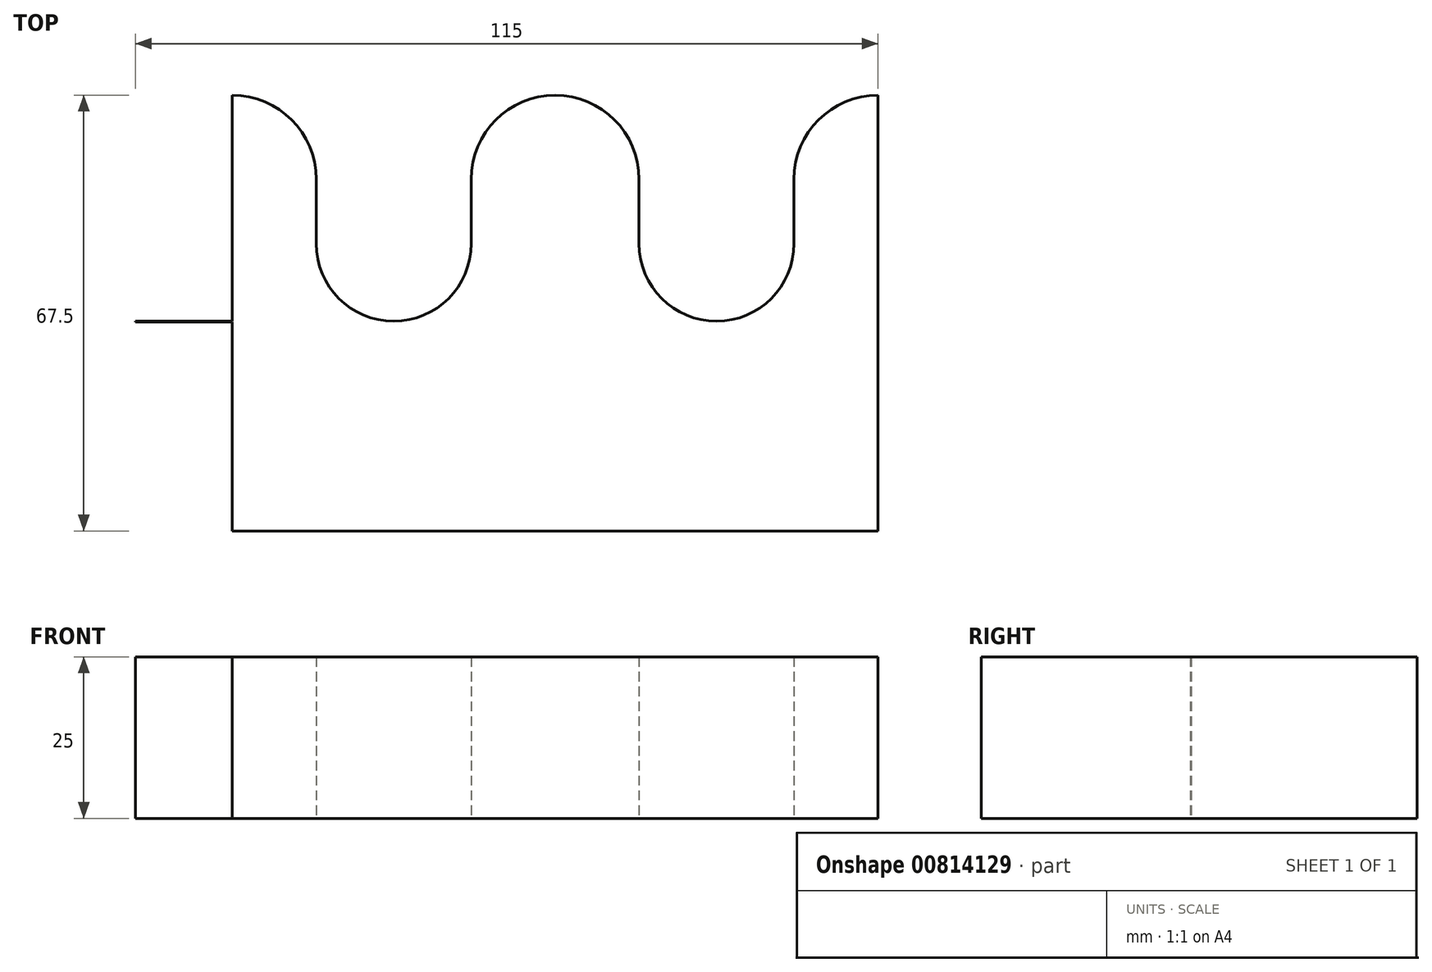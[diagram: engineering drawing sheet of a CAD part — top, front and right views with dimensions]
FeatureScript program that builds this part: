
annotation { "Feature Type Name" : "Feature", "Feature Type Description" : "" }
export const myFeature = defineFeature(function(context is Context, id is Id, definition is map)
    precondition{}
    {
        {
            var Q0;
            Q0=qCreatedBy(makeId("Top.planeOp"),FACE);
            var sketch = newSketch(context, id + "F0", { "sketchPlane" : qUnion([Q0])});
            skLineSegment(sketch, "E0", {"start": v(0, 0) * mm, "end": v(0, -67.5) * mm});
            skLineSegment(sketch, "E1", {"start": v(0, -67.5) * mm, "end": v(100, -67.5) * mm});
            skLineSegment(sketch, "E2", {"start": v(100, -67.5) * mm, "end": v(100, 0) * mm});
            skArc(sketch, "E3", {"start": v(0, 0) * mm, "mid": v(9.2, -3.8) * mm, "end": v(13, -13) * mm});
            skLineSegment(sketch, "E4", {"start": v(13, -13) * mm, "end": v(13, -23) * mm});
            skArc(sketch, "E5", {"start": v(13, -23) * mm, "mid": v(25, -35) * mm, "end": v(37, -23) * mm});
            skLineSegment(sketch, "E6", {"start": v(37, -23) * mm, "end": v(37, -13) * mm});
            skArc(sketch, "E7", {"start": v(63, -13) * mm, "mid": v(50, 0) * mm, "end": v(37, -13) * mm});
            skLineSegment(sketch, "E8", {"start": v(63, -13) * mm, "end": v(63, -23) * mm});
            skArc(sketch, "E9", {"start": v(63, -23) * mm, "mid": v(75, -35) * mm, "end": v(87, -23) * mm});
            skLineSegment(sketch, "E10", {"start": v(87, -23) * mm, "end": v(87, -13) * mm});
            skArc(sketch, "E11", {"start": v(87, -13) * mm, "mid": v(90.8, -3.8) * mm, "end": v(100, 0) * mm});
            skSolve(sketch);
        }
        {
            var Q0;
            Q0 = qSketchRegion(id + "F0", true);
            extrude(context, id + "F1", {"entities" : qUnion([Q0]), "depth" : 25 * mm, "offsetDistance" : 25 * mm});
        }
        {
            var Q0;
            Q0=qCreatedBy(makeId("Top.planeOp"),FACE);
            var sketch = newSketch(context, id + "F2", { "sketchPlane" : qUnion([Q0])});
            skLineSegment(sketch, "E12.bottom", {"start": v(0, -35) * mm, "end": v(-15, -35) * mm});
            skLineSegment(sketch, "E12.top", {"start": v(0, -35.1) * mm, "end": v(-15, -35.1) * mm});
            skLineSegment(sketch, "E12.left", {"start": v(0, -35) * mm, "end": v(0, -35.1) * mm});
            skLineSegment(sketch, "E12.right", {"start": v(-15, -35) * mm, "end": v(-15, -35.1) * mm});
            skSolve(sketch);
        }
        {
            var Q0;
            Q0 = qSketchRegion(id + "F2", true);
            extrude(context, id + "F3", {"entities" : qUnion([Q0]), "operationType" : NewBodyOperationType.ADD, "depth" : 25 * mm, "offsetDistance" : 25 * mm});
        }
    });
